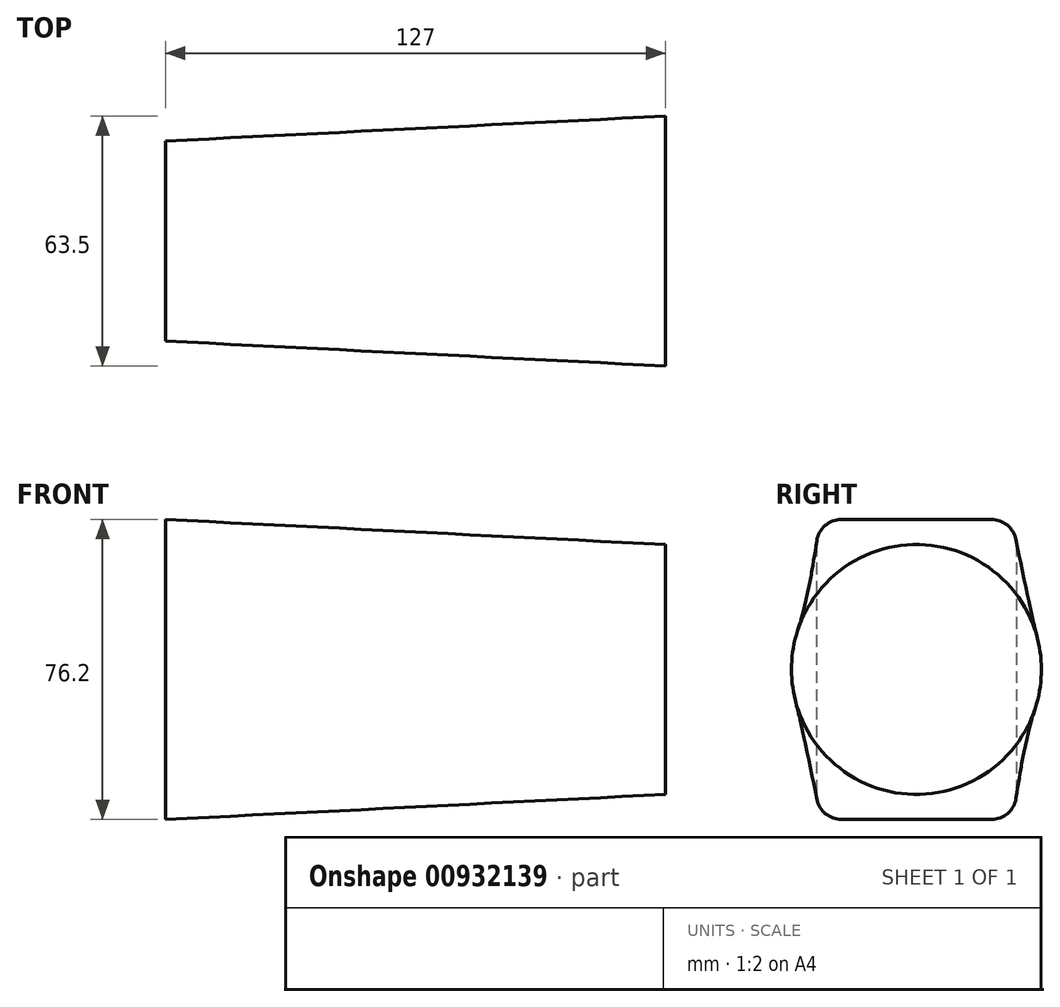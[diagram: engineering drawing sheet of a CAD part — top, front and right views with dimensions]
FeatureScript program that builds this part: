
annotation { "Feature Type Name" : "Feature", "Feature Type Description" : "" }
export const myFeature = defineFeature(function(context is Context, id is Id, definition is map)
    precondition{}
    {
        {
            var Q0;
            Q0=qCreatedBy(makeId("Right.planeOp"),FACE);
            cPlane(context, id + "F0", {"entities" : qUnion([Q0]), "cplaneType" : CPlaneType.OFFSET, "offset" : 127 * mm, "width" : 152.4 * mm, "height" : 152.4 * mm});
        }
        {
            var Q0;
            Q0=qCreatedBy(makeId("Right.planeOp"),FACE);
            var sketch = newSketch(context, id + "F1", { "sketchPlane" : qUnion([Q0])});
            skLineSegment(sketch, "E0.bottom", {"start": v(19.05, 38.1) * mm, "end": v(-19.05, 38.1) * mm});
            skLineSegment(sketch, "E0.top", {"start": v(19.05, -38.1) * mm, "end": v(-19.05, -38.1) * mm});
            skLineSegment(sketch, "E0.left", {"start": v(25.4, 31.75) * mm, "end": v(25.4, -31.75) * mm});
            skLineSegment(sketch, "E0.right", {"start": v(-25.4, 31.75) * mm, "end": v(-25.4, -31.75) * mm});
            skPoint(sketch, "E0.middle", {"position": v(0, 0) * mm});
            skPoint(sketch, "E1.visualSharp", {"position": v(-25.4, 38.1) * mm});
            skArc(sketch, "E1.filletArc", {"start": v(-19.05, 38.1) * mm, "mid": v(-23.54, 36.24) * mm, "end": v(-25.4, 31.75) * mm});
            skPoint(sketch, "E2.visualSharp", {"position": v(25.4, 38.1) * mm});
            skArc(sketch, "E2.filletArc", {"start": v(25.4, 31.75) * mm, "mid": v(23.54, 36.24) * mm, "end": v(19.05, 38.1) * mm});
            skPoint(sketch, "E3.visualSharp", {"position": v(25.4, -38.1) * mm});
            skArc(sketch, "E3.filletArc", {"start": v(19.05, -38.1) * mm, "mid": v(23.54, -36.24) * mm, "end": v(25.4, -31.75) * mm});
            skPoint(sketch, "E4.visualSharp", {"position": v(-25.4, -38.1) * mm});
            skArc(sketch, "E4.filletArc", {"start": v(-25.4, -31.75) * mm, "mid": v(-23.54, -36.24) * mm, "end": v(-19.05, -38.1) * mm});
            skSolve(sketch);
        }
        {
            var Q0;
            Q0=qCreatedBy(id+"F0.planeOp",FACE);
            var sketch = newSketch(context, id + "F2", { "sketchPlane" : qUnion([Q0])});
            skCircle(sketch, "E5", {"center": v(0, 0) * mm, "radius": 31.75 * mm});
            skSolve(sketch);
        }
        {
            var Q0;
            Q0=makeQuery(id+"F1.imprint","IMPRINT",FACE,{"disambiguationData":[TD([[makeQuery(id+"F1.imprint","IMPRINT",EDGE,{"derivedFrom":sQuery(id+"F1.wireOp",EDGE,"E0.bottom")}),1.0]])]});
            var Q1;
            Q1=makeQuery(id+"F2.imprint","IMPRINT",FACE,{"disambiguationData":[TD([[makeQuery(id+"F2.imprint","IMPRINT",EDGE,{"derivedFrom":sQuery(id+"F2.wireOp",EDGE,"E5")}),1.0]])]});
            loft(context, id + "F3", {"sheetProfilesArray" : [{ "sheetProfileEntities" : qUnion([Q0]) }, { "sheetProfileEntities" : qUnion([Q1]) }]});
        }
        {
            var Q0;
            Q0=qCreatedBy(makeId("Front.planeOp"),FACE);
            cPlane(context, id + "F4", {"entities" : qUnion([Q0]), "cplaneType" : CPlaneType.OFFSET, "offset" : 76.2 * mm, "width" : 152.4 * mm, "height" : 152.4 * mm});
        }
    });
